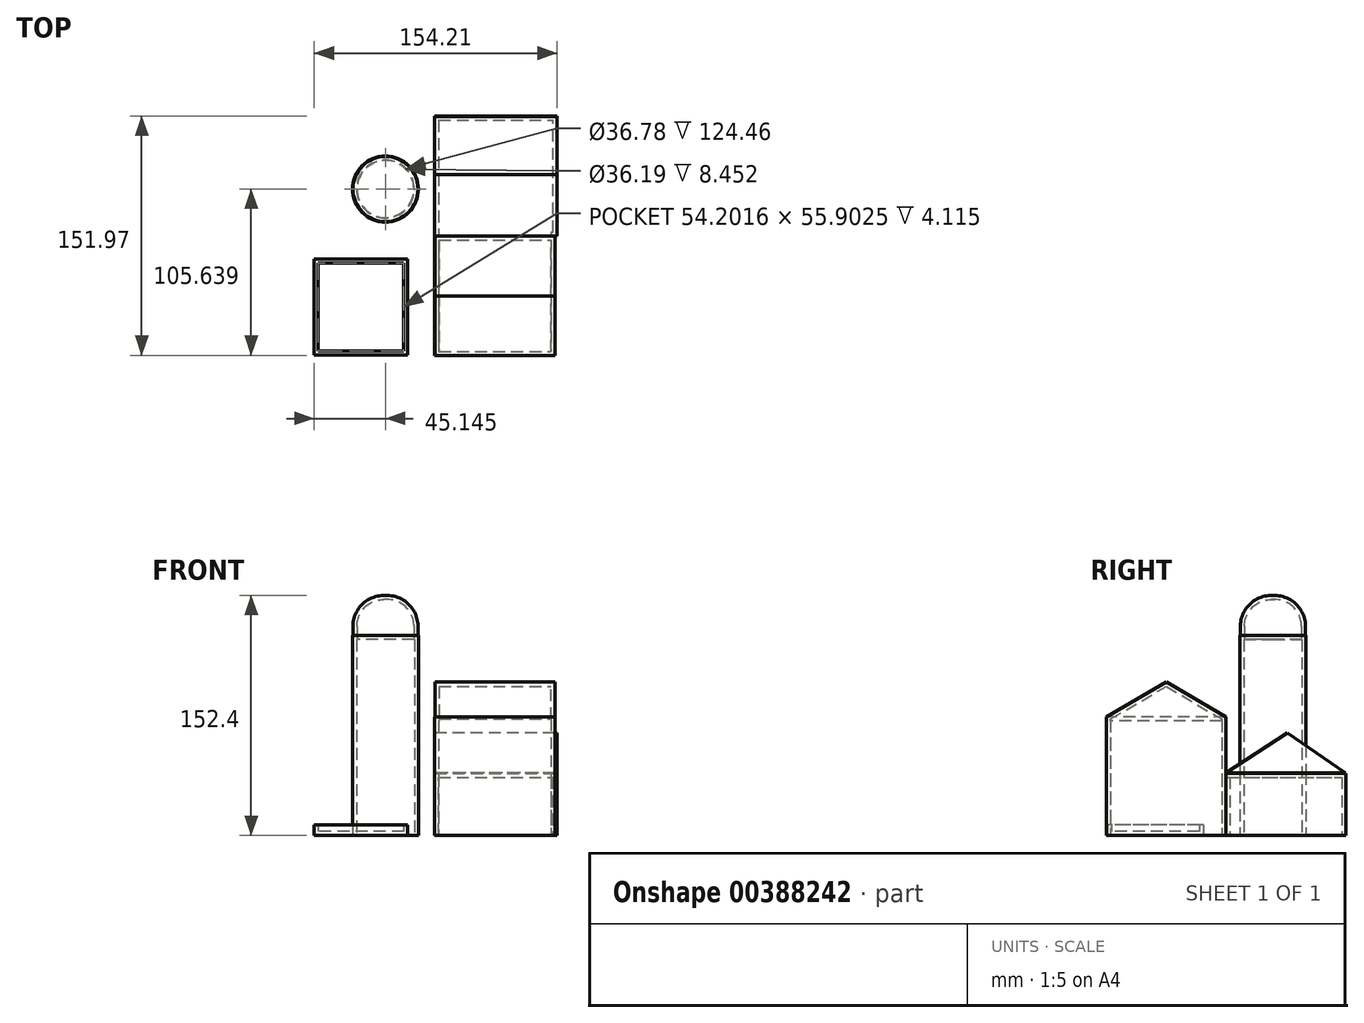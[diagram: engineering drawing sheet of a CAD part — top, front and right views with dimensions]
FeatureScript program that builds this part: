
annotation { "Feature Type Name" : "Feature", "Feature Type Description" : "" }
export const myFeature = defineFeature(function(context is Context, id is Id, definition is map)
    precondition{}
    {
        {
            var Q0;
            Q0=qCreatedBy(makeId("Top.planeOp"),FACE);
            var sketch = newSketch(context, id + "F0", { "sketchPlane" : qUnion([Q0])});
            skLineSegment(sketch, "E0.bottom", {"start": v(0, 0) * mm, "end": v(76.31, 0) * mm});
            skLineSegment(sketch, "E0.top", {"start": v(0, -75.68) * mm, "end": v(76.31, -75.68) * mm});
            skLineSegment(sketch, "E0.left", {"start": v(0, 0) * mm, "end": v(0, -75.68) * mm});
            skLineSegment(sketch, "E0.right", {"start": v(76.31, 0) * mm, "end": v(76.31, -75.68) * mm});
            skSolve(sketch);
        }
        {
            var Q0;
            Q0=makeQuery(id+"F0.imprint","IMPRINT",FACE,{"disambiguationData":[TD([[makeQuery(id+"F0.imprint","IMPRINT",EDGE,{"derivedFrom":sQuery(id+"F0.wireOp",EDGE,"E0.bottom")}),-1.0]])]});
            extrude(context, id + "F1", {"entities" : qUnion([Q0]), "depth" : 75.3 * mm});
        }
        {
            var Q0;
            Q0=makeQuery(id+"F1.opExtrude","SWEPT_FACE",FACE,{"disambiguationData":[OSD([sQuery(id+"F0.wireOp",EDGE,"E0.right")])]});
            var sketch = newSketch(context, id + "F2", { "sketchPlane" : qUnion([Q0])});
            skLineSegment(sketch, "E1", {"start": v(-37.84, 75.3) * mm, "end": v(-37.84, 97.6) * mm});
            skPoint(sketch, "E1.endSnap0", {"position": v(-37.84, 75.3) * mm});
            skLineSegment(sketch, "E2", {"start": v(-37.84, 97.6) * mm, "end": v(0, 75.3) * mm});
            skLineSegment(sketch, "E3", {"start": v(0, 75.3) * mm, "end": v(-75.68, 75.3) * mm});
            skLineSegment(sketch, "E4", {"start": v(-75.68, 75.3) * mm, "end": v(-37.84, 97.6) * mm});
            skSolve(sketch);
        }
        {
            var Q0;
            {var subQ0=sQuery(id+"F2.wireOp",EDGE,"E1");Q0=makeQuery(id+"F2.imprint","IMPRINT",FACE,{"disambiguationData":[TD([[makeQuery(id+"F2.imprint","IMPRINT",EDGE,{"derivedFrom":subQ0}),1.0]])]});}
            var Q1;
            {var subQ0=sQuery(id+"F2.wireOp",EDGE,"E1");Q1=makeQuery(id+"F2.imprint","IMPRINT",FACE,{"disambiguationData":[TD([[makeQuery(id+"F2.imprint","IMPRINT",EDGE,{"derivedFrom":subQ0}),-1.0]])]});}
            extrude(context, id + "F3", {"entities" : qUnion([Q0, Q1]), "operationType" : NewBodyOperationType.ADD, "oppositeDirection" : true, "depth" : 76.2 * mm});
        }
        {
            var Q0;
            Q0=makeQuery(id+"F1.opExtrude","CAP_FACE",FACE,{"disambiguationData":[OSD([sQuery(id+"F0.wireOp",EDGE,"E0.bottom"),sQuery(id+"F0.wireOp",EDGE,"E0.top"),sQuery(id+"F0.wireOp",EDGE,"E0.left"),sQuery(id+"F0.wireOp",EDGE,"E0.right")])],"isStart":true});
            shell(context, id + "F4", {"entities" : qUnion([Q0]), "thickness" : 2.54 * mm});
        }
        {
            var Q0;
            Q0=qCreatedBy(makeId("Top.planeOp"),FACE);
            var sketch = newSketch(context, id + "F5", { "sketchPlane" : qUnion([Q0])});
            skLineSegment(sketch, "E5.bottom", {"start": v(0, 0) * mm, "end": v(77.7, 0) * mm});
            skLineSegment(sketch, "E5.top", {"start": v(0, 76.29) * mm, "end": v(77.7, 76.29) * mm});
            skLineSegment(sketch, "E5.left", {"start": v(0, 0) * mm, "end": v(0, 76.29) * mm});
            skLineSegment(sketch, "E5.right", {"start": v(77.7, 0) * mm, "end": v(77.7, 76.29) * mm});
            skSolve(sketch);
        }
        {
            var Q0;
            Q0=makeQuery(id+"F5.imprint","IMPRINT",FACE,{"disambiguationData":[TD([[makeQuery(id+"F5.imprint","IMPRINT",EDGE,{"derivedFrom":sQuery(id+"F5.wireOp",EDGE,"E5.bottom")}),1.0]])]});
            extrude(context, id + "F6", {"entities" : qUnion([Q0]), "operationType" : NewBodyOperationType.ADD, "depth" : 39.47 * mm});
        }
        {
            var Q0;
            Q0=makeQuery(id+"F6.boolean.opBoolean","MERGE",FACE,{"derivedFrom":[makeQuery(id+"F1.opExtrude","CAP_FACE",FACE,{"disambiguationData":[OSD([sQuery(id+"F0.wireOp",EDGE,"E0.bottom"),sQuery(id+"F0.wireOp",EDGE,"E0.top"),sQuery(id+"F0.wireOp",EDGE,"E0.left"),sQuery(id+"F0.wireOp",EDGE,"E0.right")])],"isStart":true}),makeQuery(id+"F6.opExtrude","CAP_FACE",FACE,{"disambiguationData":[OSD([sQuery(id+"F5.wireOp",EDGE,"E5.bottom"),sQuery(id+"F5.wireOp",EDGE,"E5.top"),sQuery(id+"F5.wireOp",EDGE,"E5.left"),sQuery(id+"F5.wireOp",EDGE,"E5.right")])],"isStart":true})]});
            shell(context, id + "F7", {"entities" : qUnion([Q0]), "thickness" : 2.54 * mm});
        }
        {
            var Q0;
            Q0=qCreatedBy(makeId("Right.planeOp"),FACE);
            var sketch = newSketch(context, id + "F8", { "sketchPlane" : qUnion([Q0])});
            skLineSegment(sketch, "E6", {"start": v(39.1, 39.51) * mm, "end": v(39.1, 65.2) * mm});
            skLineSegment(sketch, "E7", {"start": v(39.1, 65.2) * mm, "end": v(75.87, 39.63) * mm});
            skLineSegment(sketch, "E8", {"start": v(75.87, 39.63) * mm, "end": v(0, 39.63) * mm});
            skLineSegment(sketch, "E9", {"start": v(0, 39.63) * mm, "end": v(39.1, 65.2) * mm});
            skSolve(sketch);
        }
        {
            var Q0;
            {var subQ0=sQuery(id+"F8.wireOp",EDGE,"E9");Q0=makeQuery(id+"F8.imprint","IMPRINT",FACE,{"disambiguationData":[TD([[makeQuery(id+"F8.imprint","IMPRINT",EDGE,{"derivedFrom":subQ0}),-1.0]])]});}
            var Q1;
            {var subQ0=sQuery(id+"F8.wireOp",EDGE,"E7");Q1=makeQuery(id+"F8.imprint","IMPRINT",FACE,{"disambiguationData":[TD([[makeQuery(id+"F8.imprint","IMPRINT",EDGE,{"derivedFrom":subQ0}),-1.0]])]});}
            extrude(context, id + "F9", {"entities" : qUnion([Q0, Q1]), "depth" : 77.47 * mm});
        }
        {
            var Q0;
            Q0=qCreatedBy(makeId("Top.planeOp"),FACE);
            var sketch = newSketch(context, id + "F10", { "sketchPlane" : qUnion([Q0])});
            skCircle(sketch, "E10", {"center": v(-31.37, 29.96) * mm, "radius": 20.93 * mm});
            skSolve(sketch);
        }
        {
            var Q0;
            Q0=makeQuery(id+"F10.imprint","IMPRINT",FACE,{"disambiguationData":[TD([[makeQuery(id+"F10.imprint","IMPRINT",EDGE,{"derivedFrom":sQuery(id+"F10.wireOp",EDGE,"E10")}),1.0]])]});
            extrude(context, id + "F11", {"entities" : qUnion([Q0]), "depth" : 127 * mm});
        }
        {
            var Q0;
            Q0=makeQuery(id+"F11.opExtrude","CAP_FACE",FACE,{"disambiguationData":[OSD([sQuery(id+"F10.wireOp",EDGE,"E10")])],"isStart":false});
            var sketch = newSketch(context, id + "F12", { "sketchPlane" : qUnion([Q0])});
            skCircle(sketch, "E11", {"center": v(-31.37, 29.96) * mm, "radius": 20.64 * mm});
            skSolve(sketch);
        }
        {
            var Q0;
            Q0=makeQuery(id+"F12.imprint","IMPRINT",FACE,{"disambiguationData":[TD([[makeQuery(id+"F12.imprint","IMPRINT",EDGE,{"derivedFrom":sQuery(id+"F12.wireOp",EDGE,"E11")}),1.0]])]});
            extrude(context, id + "F13", {"entities" : qUnion([Q0]), "operationType" : NewBodyOperationType.ADD, "depth" : 25.4 * mm});
        }
        {
            var Q0;
            Q0=makeQuery(id+"F13.opExtrude","CAP_EDGE",EDGE,{"disambiguationData":[OSD([sQuery(id+"F12.wireOp",EDGE,"E11")])],"isStart":false});
            fillet(context, id + "F14", {"entities" : qUnion([Q0]), "radius" : 19.49 * mm, "tangentPropagation" : true, "allowEdgeOverflow" : false});
        }
        {
            var Q0;
            Q0=makeQuery(id+"F11.opExtrude","CAP_FACE",FACE,{"disambiguationData":[OSD([sQuery(id+"F10.wireOp",EDGE,"E10")])],"isStart":true});
            shell(context, id + "F15", {"entities" : qUnion([Q0]), "thickness" : 2.54 * mm});
        }
        {
            var Q0;
            Q0=qCreatedBy(makeId("Top.planeOp"),FACE);
            var sketch = newSketch(context, id + "F16", { "sketchPlane" : qUnion([Q0])});
            skLineSegment(sketch, "E12.bottom", {"start": v(-17.23, -14.35) * mm, "end": v(-76.52, -14.35) * mm});
            skLineSegment(sketch, "E12.top", {"start": v(-17.23, -75.34) * mm, "end": v(-76.52, -75.34) * mm});
            skLineSegment(sketch, "E12.left", {"start": v(-17.23, -14.35) * mm, "end": v(-17.23, -75.34) * mm});
            skLineSegment(sketch, "E12.right", {"start": v(-76.52, -14.35) * mm, "end": v(-76.52, -75.34) * mm});
            skSolve(sketch);
        }
        {
            var Q0;
            Q0=makeQuery(id+"F16.imprint","IMPRINT",FACE,{"disambiguationData":[TD([[makeQuery(id+"F16.imprint","IMPRINT",EDGE,{"derivedFrom":sQuery(id+"F16.wireOp",EDGE,"E12.bottom")}),1.0]])]});
            extrude(context, id + "F17", {"entities" : qUnion([Q0]), "depth" : 6.65 * mm});
        }
        {
            var Q0;
            Q0=makeQuery(id+"F17.opExtrude","CAP_FACE",FACE,{"disambiguationData":[OSD([sQuery(id+"F16.wireOp",EDGE,"E12.bottom"),sQuery(id+"F16.wireOp",EDGE,"E12.top"),sQuery(id+"F16.wireOp",EDGE,"E12.left"),sQuery(id+"F16.wireOp",EDGE,"E12.right")])],"isStart":false});
            shell(context, id + "F18", {"entities" : qUnion([Q0]), "thickness" : 2.54 * mm});
        }
    });
